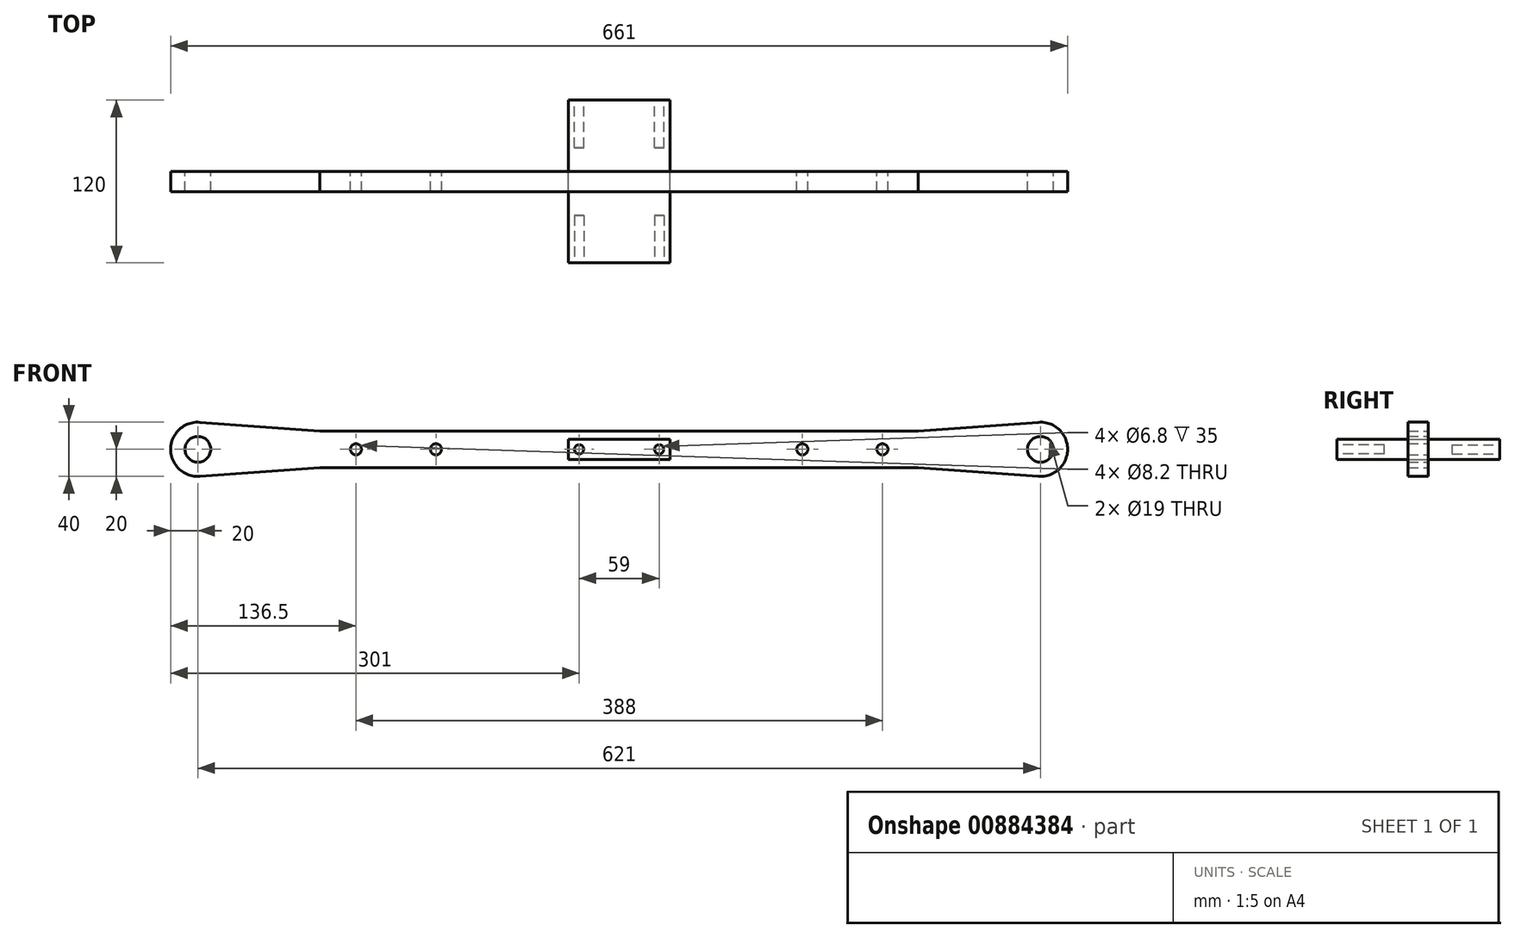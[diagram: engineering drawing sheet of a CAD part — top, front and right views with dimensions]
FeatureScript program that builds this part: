
annotation { "Feature Type Name" : "Feature", "Feature Type Description" : "" }
export const myFeature = defineFeature(function(context is Context, id is Id, definition is map)
    precondition{}
    {
        {
            var Q0;
            Q0=qCreatedBy(makeId("Front.planeOp"),FACE);
            var sketch = newSketch(context, id + "F0", { "sketchPlane" : qUnion([Q0])});
            skLineSegment(sketch, "E0.bottom", {"start": v(310.5, 13.5) * mm, "end": v(-310.5, 13.5) * mm});
            skLineSegment(sketch, "E0.top", {"start": v(310.5, -13.5) * mm, "end": v(-310.5, -13.5) * mm});
            skLineSegment(sketch, "E0.left", {"start": v(310.5, 13.5) * mm, "end": v(310.5, -13.5) * mm});
            skLineSegment(sketch, "E0.right", {"start": v(-310.5, 13.5) * mm, "end": v(-310.5, -13.5) * mm});
            skPoint(sketch, "E0.middle", {"position": v(0, 0) * mm});
            skLineSegment(sketch, "E1", {"start": v(-310.5, 0) * mm, "end": v(310.5, 0) * mm, "construction": true});
            skCircle(sketch, "E2", {"center": v(-310.5, 0) * mm, "radius": 20 * mm});
            skCircle(sketch, "E3", {"center": v(-310.5, 0) * mm, "radius": 9.5 * mm});
            skLineSegment(sketch, "E4", {"start": v(-220.5, 13.5) * mm, "end": v(-309.05, 19.95) * mm});
            skLineSegment(sketch, "E5", {"start": v(-220.5, -13.5) * mm, "end": v(-309.05, -19.95) * mm});
            skCircle(sketch, "E6", {"center": v(310.5, 0) * mm, "radius": 20 * mm});
            skCircle(sketch, "E7", {"center": v(310.5, 0) * mm, "radius": 9.5 * mm});
            skLineSegment(sketch, "E8", {"start": v(220.5, 13.5) * mm, "end": v(309.05, 19.95) * mm});
            skLineSegment(sketch, "E9", {"start": v(220.5, -13.5) * mm, "end": v(309.05, -19.95) * mm});
            skCircle(sketch, "E10", {"center": v(-194, 0) * mm, "radius": 4.1 * mm});
            skCircle(sketch, "E11", {"center": v(-135, 0) * mm, "radius": 4.1 * mm});
            skCircle(sketch, "E12", {"center": v(194, 0) * mm, "radius": 4.1 * mm});
            skCircle(sketch, "E13", {"center": v(135, 0) * mm, "radius": 4.1 * mm});
            skSolve(sketch);
        }
        {
            var Q0;
            {var subQ0=sQuery(id+"F0.wireOp",EDGE,"E0.right");var subQ5=sQuery(id+"F0.wireOp",EDGE,"E0.bottom");var subQ6=makeQuery(id+"F0.imprint","INTERSECT",VERTEX,{"derivedFrom":[subQ5,subQ0]});Q0=makeQuery(id+"F0.imprint","IMPRINT",FACE,{"disambiguationData":[TD([[makeQuery(id+"F0.imprint","IMPRINT",EDGE,{"disambiguationData":[TD([[subQ6,1.0]])],"derivedFrom":subQ5}),-1.0]])]});}
            var Q1;
            {var subQ0=sQuery(id+"F0.wireOp",EDGE,"E0.right");var subQ5=sQuery(id+"F0.wireOp",EDGE,"E0.bottom");var subQ6=makeQuery(id+"F0.imprint","INTERSECT",VERTEX,{"derivedFrom":[subQ5,subQ0]});Q1=makeQuery(id+"F0.imprint","IMPRINT",FACE,{"disambiguationData":[TD([[makeQuery(id+"F0.imprint","IMPRINT",EDGE,{"disambiguationData":[TD([[subQ6,1.0]])],"derivedFrom":subQ5}),1.0]])]});}
            var Q2;
            {var subQ0=sQuery(id+"F0.wireOp",EDGE,"E4");Q2=makeQuery(id+"F0.imprint","IMPRINT",FACE,{"disambiguationData":[TD([[makeQuery(id+"F0.imprint","IMPRINT",EDGE,{"derivedFrom":subQ0}),1.0]])]});}
            var Q3;
            {var subQ0=sQuery(id+"F0.wireOp",EDGE,"E5");Q3=makeQuery(id+"F0.imprint","IMPRINT",FACE,{"disambiguationData":[TD([[makeQuery(id+"F0.imprint","IMPRINT",EDGE,{"derivedFrom":subQ0}),-1.0]])]});}
            var Q4;
            {var subQ0=sQuery(id+"F0.wireOp",EDGE,"E0.bottom");var subQ8=makeQuery(id+"F0.imprint","INTERSECT",VERTEX,{"derivedFrom":[subQ0,sQuery(id+"F0.wireOp",EDGE,"E8")]});Q4=makeQuery(id+"F0.imprint","IMPRINT",FACE,{"disambiguationData":[TD([[makeQuery(id+"F0.imprint","IMPRINT",EDGE,{"disambiguationData":[TD([[subQ8,1.0]])],"derivedFrom":subQ0}),1.0]])]});}
            var Q5;
            {var subQ0=sQuery(id+"F0.wireOp",EDGE,"E8");Q5=makeQuery(id+"F0.imprint","IMPRINT",FACE,{"disambiguationData":[TD([[makeQuery(id+"F0.imprint","IMPRINT",EDGE,{"derivedFrom":subQ0}),-1.0]])]});}
            var Q6;
            {var subQ0=sQuery(id+"F0.wireOp",EDGE,"E9");Q6=makeQuery(id+"F0.imprint","IMPRINT",FACE,{"disambiguationData":[TD([[makeQuery(id+"F0.imprint","IMPRINT",EDGE,{"derivedFrom":subQ0}),1.0]])]});}
            var Q7;
            {var subQ0=sQuery(id+"F0.wireOp",EDGE,"E0.left");var subQ5=sQuery(id+"F0.wireOp",EDGE,"E0.bottom");var subQ6=makeQuery(id+"F0.imprint","INTERSECT",VERTEX,{"derivedFrom":[subQ5,subQ0]});Q7=makeQuery(id+"F0.imprint","IMPRINT",FACE,{"disambiguationData":[TD([[makeQuery(id+"F0.imprint","IMPRINT",EDGE,{"disambiguationData":[TD([[subQ6,-1.0]])],"derivedFrom":subQ5}),-1.0]])]});}
            var Q8;
            {var subQ0=sQuery(id+"F0.wireOp",EDGE,"E0.left");var subQ5=sQuery(id+"F0.wireOp",EDGE,"E0.bottom");var subQ6=makeQuery(id+"F0.imprint","INTERSECT",VERTEX,{"derivedFrom":[subQ5,subQ0]});Q8=makeQuery(id+"F0.imprint","IMPRINT",FACE,{"disambiguationData":[TD([[makeQuery(id+"F0.imprint","IMPRINT",EDGE,{"disambiguationData":[TD([[subQ6,-1.0]])],"derivedFrom":subQ5}),1.0]])]});}
            extrude(context, id + "F1", {"entities" : qUnion([Q0, Q1, Q2, Q3, Q4, Q5, Q6, Q7, Q8]), "endBound" : BoundingType.SYMMETRIC, "depth" : 15 * mm, "offsetDistance" : 25 * mm});
        }
        {
            var Q0;
            Q0=qCreatedBy(makeId("Front.planeOp"),FACE);
            var sketch = newSketch(context, id + "F2", { "sketchPlane" : qUnion([Q0])});
            skLineSegment(sketch, "E14.bottom", {"start": v(37.5, 7.5) * mm, "end": v(-37.5, 7.5) * mm});
            skLineSegment(sketch, "E14.top", {"start": v(37.5, -7.5) * mm, "end": v(-37.5, -7.5) * mm});
            skLineSegment(sketch, "E14.left", {"start": v(37.5, 7.5) * mm, "end": v(37.5, -7.5) * mm});
            skLineSegment(sketch, "E14.right", {"start": v(-37.5, 7.5) * mm, "end": v(-37.5, -7.5) * mm});
            skPoint(sketch, "E14.middle", {"position": v(0, 0) * mm});
            skLineSegment(sketch, "E15", {"start": v(-37.5, 0) * mm, "end": v(37.5, 0) * mm, "construction": true});
            skCircle(sketch, "E16", {"center": v(-29.5, 0) * mm, "radius": 3.4 * mm});
            skCircle(sketch, "E17", {"center": v(29.5, 0) * mm, "radius": 3.4 * mm});
            skSolve(sketch);
        }
        {
            var Q0;
            Q0=makeQuery(id+"F2.imprint","IMPRINT",FACE,{"disambiguationData":[TD([[makeQuery(id+"F2.imprint","IMPRINT",EDGE,{"derivedFrom":sQuery(id+"F2.wireOp",EDGE,"E14.bottom")}),1.0]])]});
            var Q1;
            Q1=makeQuery(id+"F2.imprint","IMPRINT",FACE,{"disambiguationData":[TD([[makeQuery(id+"F2.imprint","IMPRINT",EDGE,{"derivedFrom":sQuery(id+"F2.wireOp",EDGE,"E16")}),1.0]])]});
            var Q2;
            Q2=makeQuery(id+"F2.imprint","IMPRINT",FACE,{"disambiguationData":[TD([[makeQuery(id+"F2.imprint","IMPRINT",EDGE,{"derivedFrom":sQuery(id+"F2.wireOp",EDGE,"E17")}),1.0]])]});
            extrude(context, id + "F3", {"entities" : qUnion([Q0, Q1, Q2]), "endBound" : BoundingType.SYMMETRIC, "depth" : 120 * mm, "offsetDistance" : 25 * mm});
        }
        {
            var Q0;
            Q0=makeQuery(id+"F3.opExtrude","CAP_FACE",FACE,{"disambiguationData":[OSD([sQuery(id+"F2.wireOp",EDGE,"E14.bottom"),sQuery(id+"F2.wireOp",EDGE,"E14.top"),sQuery(id+"F2.wireOp",EDGE,"E14.left"),sQuery(id+"F2.wireOp",EDGE,"E14.right")])],"isStart":false});
            var sketch = newSketch(context, id + "F4", { "sketchPlane" : qUnion([Q0])});
            skCircle(sketch, "E18.0", {"center": v(-29.5, 0) * mm, "radius": 3.4 * mm});
            skCircle(sketch, "E18.1", {"center": v(29.5, 0) * mm, "radius": 3.4 * mm});
            skSolve(sketch);
        }
        {
            var Q0;
            Q0=makeQuery(id+"F3.opExtrude","CAP_FACE",FACE,{"disambiguationData":[OSD([sQuery(id+"F2.wireOp",EDGE,"E14.bottom"),sQuery(id+"F2.wireOp",EDGE,"E14.top"),sQuery(id+"F2.wireOp",EDGE,"E14.left"),sQuery(id+"F2.wireOp",EDGE,"E14.right")])],"isStart":true});
            var sketch = newSketch(context, id + "F5", { "sketchPlane" : qUnion([Q0])});
            skCircle(sketch, "E19.0", {"center": v(-29.5, 0) * mm, "radius": 3.4 * mm});
            skCircle(sketch, "E19.1", {"center": v(29.5, 0) * mm, "radius": 3.4 * mm});
            skSolve(sketch);
        }
        {
            var Q0;
            Q0 = qSketchRegion(id + "F4", true);
            extrude(context, id + "F6", {"entities" : qUnion([Q0]), "operationType" : NewBodyOperationType.REMOVE, "oppositeDirection" : true, "depth" : 35 * mm, "offsetDistance" : 25 * mm});
        }
        {
            var Q0;
            Q0 = qSketchRegion(id + "F5", true);
            extrude(context, id + "F7", {"entities" : qUnion([Q0]), "operationType" : NewBodyOperationType.REMOVE, "oppositeDirection" : true, "depth" : 35 * mm, "offsetDistance" : 25 * mm});
        }
    });
